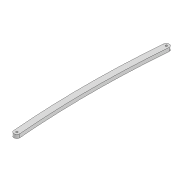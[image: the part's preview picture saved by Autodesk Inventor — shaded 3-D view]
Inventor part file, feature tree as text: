
AUTODESK INVENTOR PART (.ipt)
format: ipt  version: 2022 (Build 260153000, 153)  size: 93,696 bytes
history: native  units: mm
features: extrude x1, sketch x1
ambient origin geometry x8: Origin, YZ Plane, XZ Plane, XY Plane, X Axis, Y Axis, Z Axis, Center Point
bodies: Solid1 (feature_tree)
feature tree (2):
  extrude  "Extrusion1"  Depth=1500.0mm
  sketch  "Sketch1"  dims[d0=3.3mm d1=3.3mm d2=10.0mm d3=253.429mm d6=6.0mm d7=0.0mm d16=1500.0mm d17=1500.0mm]
